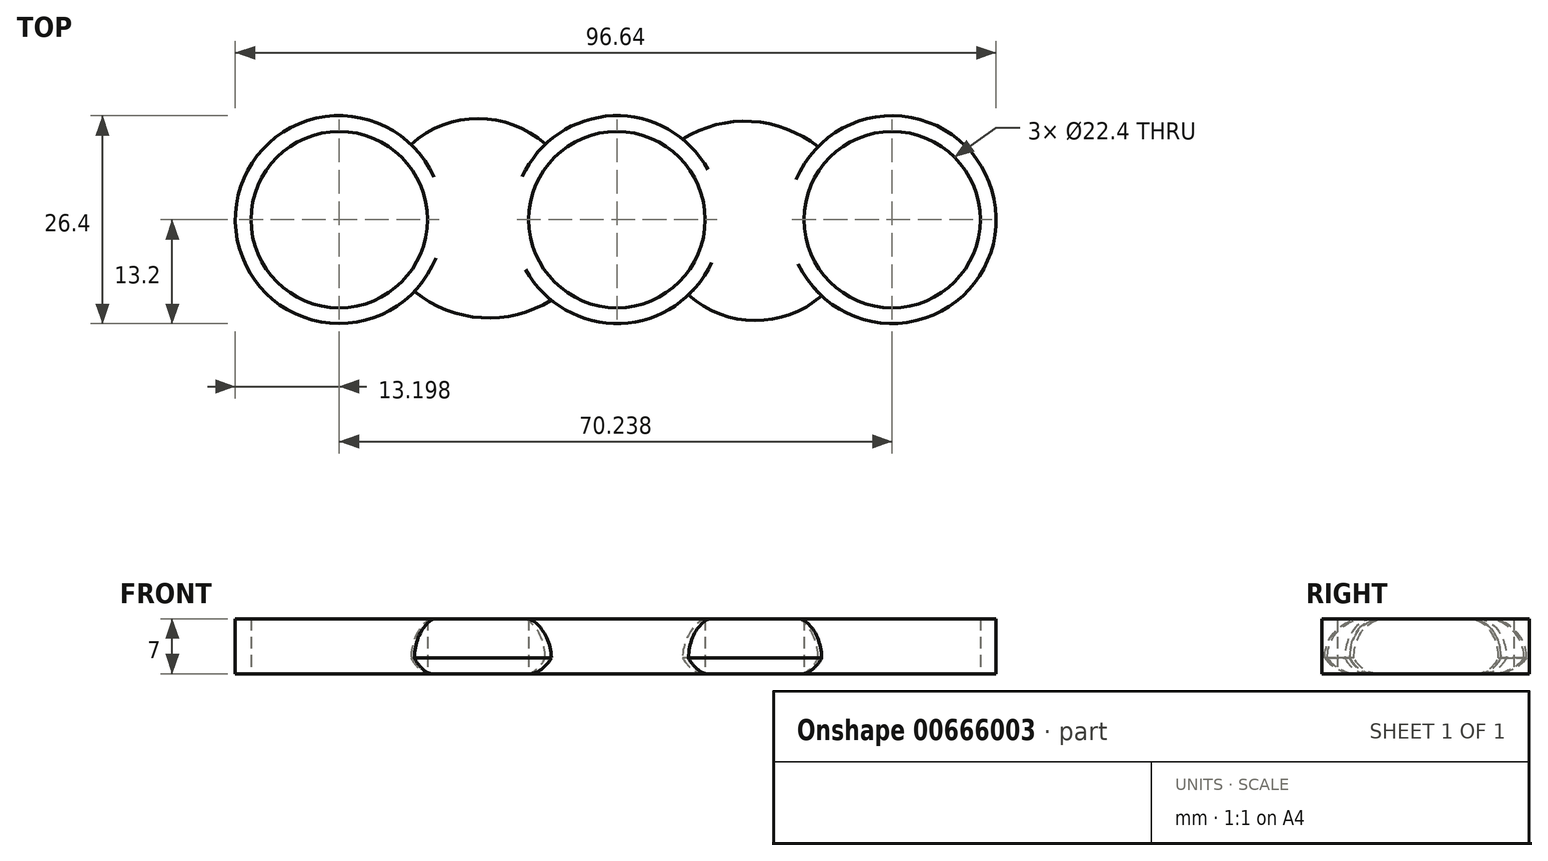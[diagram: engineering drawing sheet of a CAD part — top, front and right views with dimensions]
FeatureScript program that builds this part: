
annotation { "Feature Type Name" : "Feature", "Feature Type Description" : "" }
export const myFeature = defineFeature(function(context is Context, id is Id, definition is map)
    precondition{}
    {
        {
            var Q0;
            Q0=qCreatedBy(makeId("Top.planeOp"),FACE);
            var sketch = newSketch(context, id + "F0", { "sketchPlane" : qUnion([Q0])});
            skCircle(sketch, "E0", {"center": v(0, 0) * mm, "radius": 11.2 * mm});
            skArc(sketch, "E1", {"start": v(-8.33, -10.24) * mm, "mid": v(0.5, -13.2) * mm, "end": v(9.1, -9.57) * mm});
            skCircle(sketch, "E2", {"center": v(-35.27, 0) * mm, "radius": 11.2 * mm});
            skArc(sketch, "E3", {"start": v(-26.16, 9.55) * mm, "mid": v(-48.47, -0.31) * mm, "end": v(-25.72, -9.11) * mm});
            skCircle(sketch, "E4", {"center": v(34.97, 0) * mm, "radius": 11.2 * mm});
            skArc(sketch, "E5", {"start": v(26, -9.7) * mm, "mid": v(48.16, 0.32) * mm, "end": v(25.55, 9.25) * mm});
            skArc(sketch, "E6", {"start": v(-25.72, -9.11) * mm, "mid": v(-17.2, -12.46) * mm, "end": v(-8.33, -10.24) * mm});
            skArc(sketch, "E7.1.0", {"start": v(25.72, 9.11) * mm, "mid": v(17.2, 12.46) * mm, "end": v(8.33, 10.24) * mm});
            skArc(sketch, "E8", {"start": v(-9.1, 9.57) * mm, "mid": v(-17.63, 12.82) * mm, "end": v(-26.16, 9.55) * mm});
            skArc(sketch, "E9.1.0", {"start": v(9.1, -9.57) * mm, "mid": v(17.63, -12.82) * mm, "end": v(26.16, -9.55) * mm});
            skArc(sketch, "E10.trimOffspring", {"start": v(8.33, 10.24) * mm, "mid": v(-0.5, 13.2) * mm, "end": v(-9.1, 9.57) * mm});
            skSolve(sketch);
        }
        {
            var Q0;
            Q0=makeQuery(id+"F0.imprint","IMPRINT",FACE,{"disambiguationData":[TD([[makeQuery(id+"F0.imprint","IMPRINT",EDGE,{"derivedFrom":sQuery(id+"F0.wireOp",EDGE,"E0")}),-1.0]])]});
            extrude(context, id + "F1", {"entities" : qUnion([Q0]), "depth" : 7 * mm, "offsetDistance" : 25 * mm});
        }
        {
            var Q0;
            Q0=makeQuery(id+"F1.opExtrude","CAP_EDGE",EDGE,{"disambiguationData":[OSD([sQuery(id+"F0.wireOp",EDGE,"E8")])],"isStart":false});
            fillet(context, id + "F2", {"entities" : qUnion([Q0]), "tangentPropagation" : true, "radius" : 5 * mm, "defaultsChanged" : false, "vertexSettings" : [], "allowEdgeOverflow" : false});
        }
        {
            var Q0;
            Q0=makeQuery(id+"F1.opExtrude","CAP_EDGE",EDGE,{"disambiguationData":[OSD([sQuery(id+"F0.wireOp",EDGE,"E7.1.0")])],"isStart":false});
            fillet(context, id + "F3", {"entities" : qUnion([Q0]), "tangentPropagation" : true, "radius" : 5 * mm, "defaultsChanged" : false, "vertexSettings" : [], "allowEdgeOverflow" : false});
        }
        {
            var Q0;
            Q0=makeQuery(id+"F1.opExtrude","CAP_EDGE",EDGE,{"disambiguationData":[OSD([sQuery(id+"F0.wireOp",EDGE,"E6")])],"isStart":false});
            fillet(context, id + "F4", {"entities" : qUnion([Q0]), "tangentPropagation" : true, "radius" : 5 * mm, "defaultsChanged" : false, "vertexSettings" : [], "allowEdgeOverflow" : false});
        }
        {
            var Q0;
            Q0=makeQuery(id+"F1.opExtrude","CAP_EDGE",EDGE,{"disambiguationData":[OSD([sQuery(id+"F0.wireOp",EDGE,"E9.1.0")])],"isStart":false});
            fillet(context, id + "F5", {"entities" : qUnion([Q0]), "tangentPropagation" : true, "radius" : 5 * mm, "defaultsChanged" : false, "vertexSettings" : [], "allowEdgeOverflow" : false});
        }
        {
            var Q0;
            Q0=makeQuery(id+"F1.opExtrude","CAP_EDGE",EDGE,{"disambiguationData":[OSD([sQuery(id+"F0.wireOp",EDGE,"E6")])],"isStart":true});
            fillet(context, id + "F6", {"entities" : qUnion([Q0]), "tangentPropagation" : true, "radius" : 5 * mm, "defaultsChanged" : false, "vertexSettings" : [], "allowEdgeOverflow" : false});
        }
        {
            var Q0;
            Q0=makeQuery(id+"F1.opExtrude","CAP_EDGE",EDGE,{"disambiguationData":[OSD([sQuery(id+"F0.wireOp",EDGE,"E9.1.0")])],"isStart":true});
            fillet(context, id + "F7", {"entities" : qUnion([Q0]), "tangentPropagation" : true, "radius" : 5 * mm, "defaultsChanged" : false, "vertexSettings" : [], "allowEdgeOverflow" : false});
        }
        {
            var Q0;
            Q0=makeQuery(id+"F1.opExtrude","CAP_EDGE",EDGE,{"disambiguationData":[OSD([sQuery(id+"F0.wireOp",EDGE,"E8")])],"isStart":true});
            fillet(context, id + "F8", {"entities" : qUnion([Q0]), "tangentPropagation" : true, "radius" : 5 * mm, "defaultsChanged" : false, "vertexSettings" : [], "allowEdgeOverflow" : false});
        }
        {
            var Q0;
            Q0=makeQuery(id+"F1.opExtrude","CAP_EDGE",EDGE,{"disambiguationData":[OSD([sQuery(id+"F0.wireOp",EDGE,"E7.1.0")])],"isStart":true});
            fillet(context, id + "F9", {"entities" : qUnion([Q0]), "tangentPropagation" : true, "radius" : 5 * mm, "defaultsChanged" : false, "vertexSettings" : [], "allowEdgeOverflow" : false});
        }
    });
